# Revit family: KEUCO_14907010000_
name_source: partatom
category: Generic Models
revit_build: Autodesk Revit 2016 (Build: 20150220_1215(x64)
units: mm (PartAtom-declared; Revit-internal decimal feet)

## family parameters
Always vertical = No
Can host rebar = No
Cut with Voids When Loaded = No
Part Type = Normal
Room Calculation Point = No
Round Connector Dimension = Use Diameter
Shared = No
Work Plane-Based = Yes

## types (3) — shared parameters
Default Elevation = 1219 mm
Description = --
Manufacturer = KEUCO
Rail Length = 351 mm  [stored 1.15157 ft]
Serie = Plan
URL = https://www.keuco.com
Verwendung = BI / DU / WA
zero-valued in all types: Gewicht

## per-type parameters (varying)
| type | Ausschreibungstext | Stange Material |
| 14907010000 | KEUCO PLAN Haltegriff 14907010000
Hochglanzverchromter Haltegriff 
in ästhetischem, funktionalem Design
bis 115 kg belastbar, antistatisch, leicht zu reinigen
Achsmaß 300 mm, bei einer Gesamtbreite von 351 mm
Ausladung 67 mm
Baumuster geprüft
Der Haltegriff wird verdeckt angebracht
Lieferung inkl. korrosionsfreiem Befestigungsmaterial | Verchromt |
| 14907070000 | KEUCO PLAN Haltegriff 14907070000
Haltegriff aus hochwertigem Edelstahl
in ästhetischem, funktionalem Design
bis 115 kg belastbar, antistatisch, leicht zu reinigen
Achsmaß 300 mm, bei einer Gesamtbreite von 351 mm
Ausladung 67 mm
Baumuster geprüft
Der Haltegriff wird verdeckt angebracht
Lieferung inkl. korrosionsfreiem Befestigungsmaterial | Edelstahl |
| 14907170000 | KEUCO PLAN Haltegriff 14907170000
Eleganter Haltegriff 
aus silber-eloxiertem Aluminium (E6 EV1)/verchromt in
ästhetischem, funktionalem Design
bis 115 kg belastbar, antistatisch, leicht zu reinigen
Die Wandhalterungen sind als Design-Element hochglanzverchromt
Achsmaß 300 mm, bei einer Gesamtbreite von 351 mm
Ausladung 67 mm
Baumuster geprüft
Der Haltegriff wird verdeckt angebracht
Lieferung inkl. korrosionsfreiem Befestigungsmaterial | Aluminium silber-eloxiert (E6 EV1) |

note: column(s) folded — value = type name in every type: Artikelnummer

note: [stored X ft] marks values corroborated as IEEE doubles in the binary element streams (Revit-internal decimal feet)

## geometry (parser evidence)
native form markers: Sweep x2
no freeform markers — native parametric forms only
